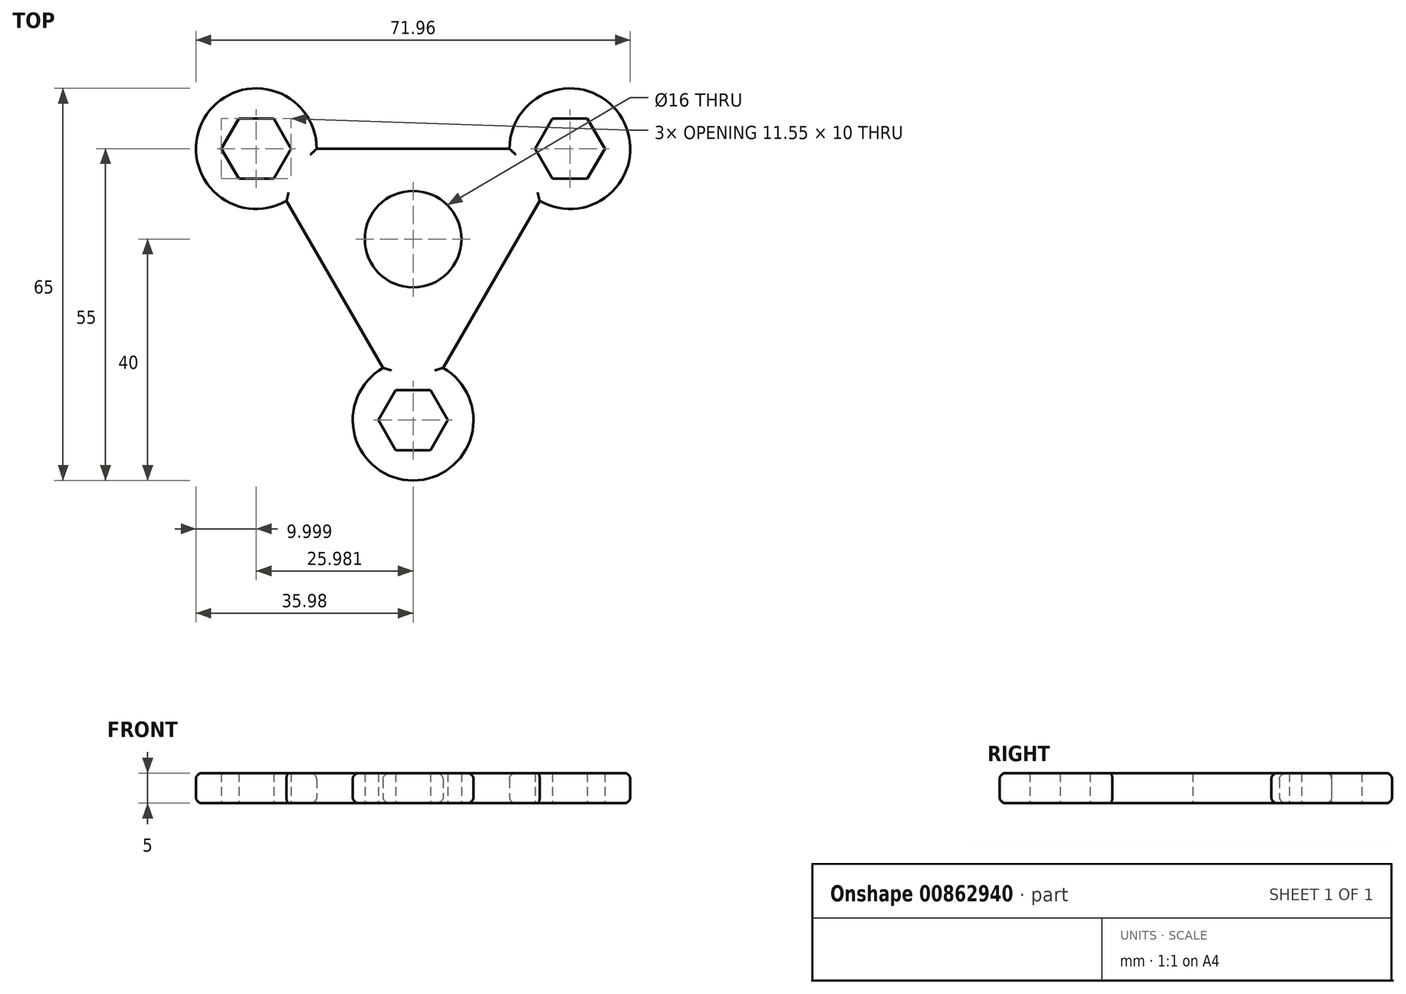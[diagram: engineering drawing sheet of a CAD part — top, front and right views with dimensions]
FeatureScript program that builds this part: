
annotation { "Feature Type Name" : "Feature", "Feature Type Description" : "" }
export const myFeature = defineFeature(function(context is Context, id is Id, definition is map)
    precondition{}
    {
        {
            var Q0;
            Q0=qCreatedBy(makeId("Top.planeOp"),FACE);
            var sketch = newSketch(context, id + "F0", { "sketchPlane" : qUnion([Q0])});
            skLineSegment(sketch, "E0.0", {"start": v(-20.98, 15) * mm, "end": v(-20.2, 15) * mm, "construction": true});
            skLineSegment(sketch, "E0.1", {"start": v(25.98, 15) * mm, "end": v(23.1, 10) * mm, "construction": true});
            skLineSegment(sketch, "E0.2", {"start": v(0, -30) * mm, "end": v(-2.89, -25) * mm, "construction": true});
            skCircle(sketch, "E1", {"center": v(0, 0) * mm, "radius": 8 * mm});
            skCircle(sketch, "E2.cCircle", {"center": v(-25.98, 15) * mm, "radius": 5 * mm, "construction": true});
            skLineSegment(sketch, "E2.0", {"start": v(-28.87, 20) * mm, "end": v(-23.1, 20) * mm});
            skLineSegment(sketch, "E2.1", {"start": v(-23.1, 20) * mm, "end": v(-20.2, 15) * mm});
            skLineSegment(sketch, "E2.2", {"start": v(-20.2, 15) * mm, "end": v(-23.1, 10) * mm});
            skLineSegment(sketch, "E2.3", {"start": v(-23.1, 10) * mm, "end": v(-28.87, 10) * mm});
            skLineSegment(sketch, "E2.4", {"start": v(-28.87, 10) * mm, "end": v(-31.75, 15) * mm});
            skLineSegment(sketch, "E2.5", {"start": v(-31.75, 15) * mm, "end": v(-28.87, 20) * mm});
            skPoint(sketch, "E2.0.midPoint", {"position": v(-25.98, 20) * mm});
            skCircle(sketch, "E3.cCircle", {"center": v(25.98, 15) * mm, "radius": 5 * mm, "construction": true});
            skLineSegment(sketch, "E3.0", {"start": v(23.1, 20) * mm, "end": v(28.87, 20) * mm});
            skLineSegment(sketch, "E3.1", {"start": v(28.87, 20) * mm, "end": v(31.75, 15) * mm});
            skLineSegment(sketch, "E3.2", {"start": v(31.75, 15) * mm, "end": v(28.87, 10) * mm});
            skLineSegment(sketch, "E3.3", {"start": v(28.87, 10) * mm, "end": v(23.1, 10) * mm});
            skLineSegment(sketch, "E3.4", {"start": v(23.1, 10) * mm, "end": v(20.2, 15) * mm});
            skLineSegment(sketch, "E3.5", {"start": v(20.2, 15) * mm, "end": v(23.1, 20) * mm});
            skPoint(sketch, "E3.0.midPoint", {"position": v(25.98, 20) * mm});
            skCircle(sketch, "E4.cCircle", {"center": v(0, -30) * mm, "radius": 5 * mm, "construction": true});
            skLineSegment(sketch, "E4.0", {"start": v(-2.89, -25) * mm, "end": v(2.89, -25) * mm});
            skLineSegment(sketch, "E4.1", {"start": v(2.89, -25) * mm, "end": v(5.77, -30) * mm});
            skLineSegment(sketch, "E4.2", {"start": v(5.77, -30) * mm, "end": v(2.89, -35) * mm});
            skLineSegment(sketch, "E4.3", {"start": v(2.89, -35) * mm, "end": v(-2.89, -35) * mm});
            skLineSegment(sketch, "E4.4", {"start": v(-2.89, -35) * mm, "end": v(-5.77, -30) * mm});
            skLineSegment(sketch, "E4.5", {"start": v(-5.77, -30) * mm, "end": v(-2.89, -25) * mm});
            skPoint(sketch, "E4.0.midPoint", {"position": v(0, -25) * mm});
            skCircle(sketch, "E5", {"center": v(-25.98, 15) * mm, "radius": 10 * mm});
            skCircle(sketch, "E6", {"center": v(25.98, 15) * mm, "radius": 10 * mm});
            skCircle(sketch, "E7", {"center": v(0, -30) * mm, "radius": 10 * mm});
            skLineSegment(sketch, "E8.trimOffspring", {"start": v(-23.1, 10) * mm, "end": v(-23.48, 10.67) * mm, "construction": true});
            skLineSegment(sketch, "E9.trimOffspring", {"start": v(20.2, 15) * mm, "end": v(25.98, 15) * mm, "construction": true});
            skLineSegment(sketch, "E10.trimOffspring", {"start": v(2.89, -25) * mm, "end": v(0, -30) * mm, "construction": true});
            skCircle(sketch, "E11.cCircle", {"center": v(0, 0) * mm, "radius": 15 * mm, "construction": true});
            skLineSegment(sketch, "E11.0", {"start": v(-25.98, 15) * mm, "end": v(-20.2, 15) * mm});
            skLineSegment(sketch, "E11.1", {"start": v(25.98, 15) * mm, "end": v(0, -30) * mm});
            skLineSegment(sketch, "E11.2", {"start": v(0, -30) * mm, "end": v(-20.98, 6.34) * mm});
            skPoint(sketch, "E11.0.midPoint", {"position": v(0, 15) * mm});
            skLineSegment(sketch, "E12.trimOffspring", {"start": v(-15.98, 15) * mm, "end": v(25.98, 15) * mm});
            skLineSegment(sketch, "E13.trimOffspring", {"start": v(-23.1, 10) * mm, "end": v(-25.98, 15) * mm});
            skSolve(sketch);
        }
        {
            var Q0;
            {var subQ0=sQuery(id+"F0.wireOp",EDGE,"E4.1");Q0=makeQuery(id+"F0.imprint","IMPRINT",FACE,{"disambiguationData":[TD([[makeQuery(id+"F0.imprint","IMPRINT",EDGE,{"derivedFrom":subQ0}),1.0]])]});}
            var Q1;
            Q1=makeQuery(id+"F0.imprint","IMPRINT",FACE,{"disambiguationData":[TD([[makeQuery(id+"F0.imprint","IMPRINT",EDGE,{"derivedFrom":sQuery(id+"F0.wireOp",EDGE,"E1")}),-1.0]])]});
            var Q2;
            Q2=makeQuery(id+"F0.imprint","IMPRINT",FACE,{"disambiguationData":[TD([[makeQuery(id+"F0.imprint","IMPRINT",EDGE,{"derivedFrom":sQuery(id+"F0.wireOp",EDGE,"E2.0")}),1.0]])]});
            var Q3;
            Q3=makeQuery(id+"F0.imprint","IMPRINT",FACE,{"disambiguationData":[TD([[makeQuery(id+"F0.imprint","IMPRINT",EDGE,{"derivedFrom":sQuery(id+"F0.wireOp",EDGE,"E3.0")}),1.0]])]});
            var Q4;
            {var subQ0=sQuery(id+"F0.wireOp",EDGE,"E4.0");Q4=makeQuery(id+"F0.imprint","IMPRINT",FACE,{"disambiguationData":[TD([[makeQuery(id+"F0.imprint","IMPRINT",EDGE,{"derivedFrom":subQ0}),1.0]])]});}
            var Q5;
            {var subQ0=sQuery(id+"F0.wireOp",EDGE,"E3.4");Q5=makeQuery(id+"F0.imprint","IMPRINT",FACE,{"disambiguationData":[TD([[makeQuery(id+"F0.imprint","IMPRINT",EDGE,{"derivedFrom":subQ0}),1.0]])]});}
            extrude(context, id + "F1", {"entities" : qUnion([Q0, Q1, Q2, Q3, Q4, Q5]), "depth" : 5 * mm, "offsetDistance" : 25 * mm});
        }
        {
            var Q0;
            Q0=makeQuery(id+"F1.opExtrude","CAP_EDGE",EDGE,{"disambiguationData":[OSD([sQuery(id+"F0.wireOp",EDGE,"E5")])],"isStart":false});
            var Q1;
            Q1=makeQuery(id+"F1.opExtrude","CAP_EDGE",EDGE,{"disambiguationData":[OSD([sQuery(id+"F0.wireOp",EDGE,"E12.trimOffspring")])],"isStart":false});
            var Q2;
            Q2=makeQuery(id+"F1.opExtrude","CAP_EDGE",EDGE,{"disambiguationData":[OSD([sQuery(id+"F0.wireOp",EDGE,"E6")])],"isStart":false});
            var Q3;
            Q3=makeQuery(id+"F1.opExtrude","CAP_EDGE",EDGE,{"disambiguationData":[OSD([sQuery(id+"F0.wireOp",EDGE,"E11.1")])],"isStart":false});
            var Q4;
            Q4=makeQuery(id+"F1.opExtrude","CAP_EDGE",EDGE,{"disambiguationData":[OSD([sQuery(id+"F0.wireOp",EDGE,"E7")])],"isStart":false});
            var Q5;
            Q5=makeQuery(id+"F1.opExtrude","CAP_EDGE",EDGE,{"disambiguationData":[OSD([sQuery(id+"F0.wireOp",EDGE,"E11.2")])],"isStart":false});
            var Q6;
            Q6=makeQuery(id+"F1.opExtrude","CAP_EDGE",EDGE,{"disambiguationData":[OSD([sQuery(id+"F0.wireOp",EDGE,"E11.1")])],"isStart":true});
            var Q7;
            Q7=makeQuery(id+"F1.opExtrude","CAP_EDGE",EDGE,{"disambiguationData":[OSD([sQuery(id+"F0.wireOp",EDGE,"E6")])],"isStart":true});
            var Q8;
            Q8=makeQuery(id+"F1.opExtrude","CAP_EDGE",EDGE,{"disambiguationData":[OSD([sQuery(id+"F0.wireOp",EDGE,"E12.trimOffspring")])],"isStart":true});
            var Q9;
            Q9=makeQuery(id+"F1.opExtrude","CAP_EDGE",EDGE,{"disambiguationData":[OSD([sQuery(id+"F0.wireOp",EDGE,"E5")])],"isStart":true});
            var Q10;
            Q10=makeQuery(id+"F1.opExtrude","CAP_EDGE",EDGE,{"disambiguationData":[OSD([sQuery(id+"F0.wireOp",EDGE,"E7")])],"isStart":true});
            var Q11;
            Q11=makeQuery(id+"F1.opExtrude","CAP_EDGE",EDGE,{"disambiguationData":[OSD([sQuery(id+"F0.wireOp",EDGE,"E11.2")])],"isStart":true});
            fillet(context, id + "F2", {"entities" : qUnion([Q0, Q1, Q2, Q3, Q4, Q5, Q6, Q7, Q8, Q9, Q10, Q11]), "radius" : 1 * mm, "tangentPropagation" : true, "allowEdgeOverflow" : false});
        }
    });
